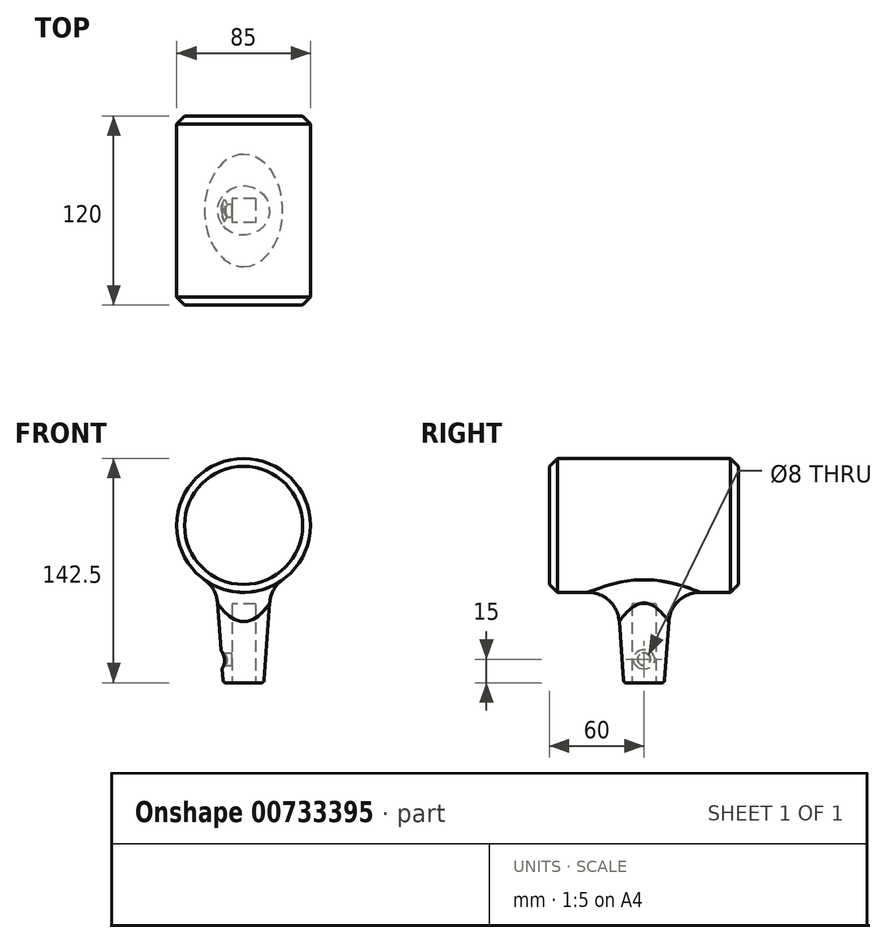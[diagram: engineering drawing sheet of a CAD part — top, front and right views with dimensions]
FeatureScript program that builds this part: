
annotation { "Feature Type Name" : "Feature", "Feature Type Description" : "" }
export const myFeature = defineFeature(function(context is Context, id is Id, definition is map)
    precondition{}
    {
        {
            var Q0;
            Q0=qCreatedBy(makeId("Front.planeOp"),FACE);
            var sketch = newSketch(context, id + "F0", { "sketchPlane" : qUnion([Q0])});
            skCircle(sketch, "E0", {"center": v(0, 0) * mm, "radius": 42.5 * mm});
            skSolve(sketch);
        }
        {
            var Q0;
            Q0=makeQuery(id+"F0.imprint","IMPRINT",FACE,{"disambiguationData":[TD([[makeQuery(id+"F0.imprint","IMPRINT",EDGE,{"derivedFrom":sQuery(id+"F0.wireOp",EDGE,"E0")}),1.0]])]});
            extrude(context, id + "F1", {"entities" : qUnion([Q0]), "endBound" : BoundingType.SYMMETRIC, "depth" : 120 * mm, "offsetDistance" : 25 * mm});
        }
        {
            var Q0;
            Q0=qCreatedBy(makeId("Top.planeOp"),FACE);
            var sketch = newSketch(context, id + "F2", { "sketchPlane" : qUnion([Q0])});
            skCircle(sketch, "E1", {"center": v(0, 0) * mm, "radius": 20 * mm});
            skSolve(sketch);
        }
        {
            var Q0;
            Q0 = qSketchRegion(id + "F2", true);
            extrude(context, id + "F3", {"entities" : qUnion([Q0]), "operationType" : NewBodyOperationType.ADD, "oppositeDirection" : true, "depth" : 100 * mm, "offsetDistance" : 25 * mm, "hasDraft" : true, "draftAngle" : 4 * degree, "draftPullDirection" : true});
        }
        {
            var Q0;
            Q0=makeQuery(id+"F3.opExtrude","CAP_FACE",FACE,{"disambiguationData":[OSD([sQuery(id+"F2.wireOp",EDGE,"E1")])],"isStart":false});
            var sketch = newSketch(context, id + "F4", { "sketchPlane" : qUnion([Q0])});
            skLineSegment(sketch, "E2.bottom", {"start": v(7.5, -7.5) * mm, "end": v(-7.5, -7.5) * mm});
            skLineSegment(sketch, "E2.top", {"start": v(7.5, 7.5) * mm, "end": v(-7.5, 7.5) * mm});
            skLineSegment(sketch, "E2.left", {"start": v(7.5, -7.5) * mm, "end": v(7.5, 7.5) * mm});
            skLineSegment(sketch, "E2.right", {"start": v(-7.5, -7.5) * mm, "end": v(-7.5, 7.5) * mm});
            skPoint(sketch, "E2.middle", {"position": v(0, 0) * mm});
            skSolve(sketch);
        }
        {
            var Q0;
            Q0 = qSketchRegion(id + "F4", true);
            extrude(context, id + "F5", {"entities" : qUnion([Q0]), "operationType" : NewBodyOperationType.REMOVE, "oppositeDirection" : true, "depth" : 50 * mm, "offsetDistance" : 25 * mm});
        }
        {
            var Q0;
            Q0=qCreatedBy(makeId("Right.planeOp"),FACE);
            var sketch = newSketch(context, id + "F6", { "sketchPlane" : qUnion([Q0])});
            skCircle(sketch, "E3", {"center": v(0, -85) * mm, "radius": 4 * mm});
            skSolve(sketch);
        }
        {
            var Q0;
            Q0 = qSketchRegion(id + "F6", true);
            extrude(context, id + "F7", {"entities" : qUnion([Q0]), "operationType" : NewBodyOperationType.REMOVE, "oppositeDirection" : true, "depth" : 50 * mm, "offsetDistance" : 25 * mm});
        }
        {
            var Q0;
            Q0=makeQuery(id+"F1.opExtrude","CAP_FACE",FACE,{"disambiguationData":[OSD([sQuery(id+"F0.wireOp",EDGE,"E0")])],"isStart":true});
            var Q1;
            Q1=makeQuery(id+"F1.opExtrude","CAP_FACE",FACE,{"disambiguationData":[OSD([sQuery(id+"F0.wireOp",EDGE,"E0")])],"isStart":false});
            chamfer(context, id + "F8", {"entities" : qUnion([Q0, Q1]), "width" : 5 * mm, "tangentPropagation" : true});
        }
        {
            var Q0;
            Q0=makeQuery(id+"F3.boolean.opBoolean","INTERSECT",EDGE,{"derivedFrom":[makeQuery(id+"F1.opExtrude","SWEPT_FACE",FACE,{"disambiguationData":[OSD([sQuery(id+"F0.wireOp",EDGE,"E0")])]}),makeQuery(id+"F3.opExtrude","SWEPT_FACE",FACE,{"disambiguationData":[OSD([sQuery(id+"F2.wireOp",EDGE,"E1")])]})]});
            fillet(context, id + "F9", {"entities" : qUnion([Q0]), "radius" : 20 * mm, "tangentPropagation" : true, "allowEdgeOverflow" : false});
        }
        {
            var Q0;
            Q0=makeQuery(id+"F3.opExtrude","CAP_EDGE",EDGE,{"disambiguationData":[OSD([sQuery(id+"F2.wireOp",EDGE,"E1")])],"isStart":false});
            fillet(context, id + "F10", {"entities" : qUnion([Q0]), "radius" : 2 * mm, "tangentPropagation" : true, "allowEdgeOverflow" : false});
        }
        {
            var Q0;
            Q0=makeQuery(id+"F7.boolean.opBoolean","INTERSECT",EDGE,{"derivedFrom":[makeQuery(id+"F3.opExtrude","SWEPT_FACE",FACE,{"disambiguationData":[OSD([sQuery(id+"F2.wireOp",EDGE,"E1")])]}),makeQuery(id+"F7.opExtrude","SWEPT_FACE",FACE,{"disambiguationData":[OSD([sQuery(id+"F6.wireOp",EDGE,"E3")])]})]});
            chamfer(context, id + "F11", {"entities" : qUnion([Q0]), "width" : 2 * mm, "tangentPropagation" : true});
        }
    });
